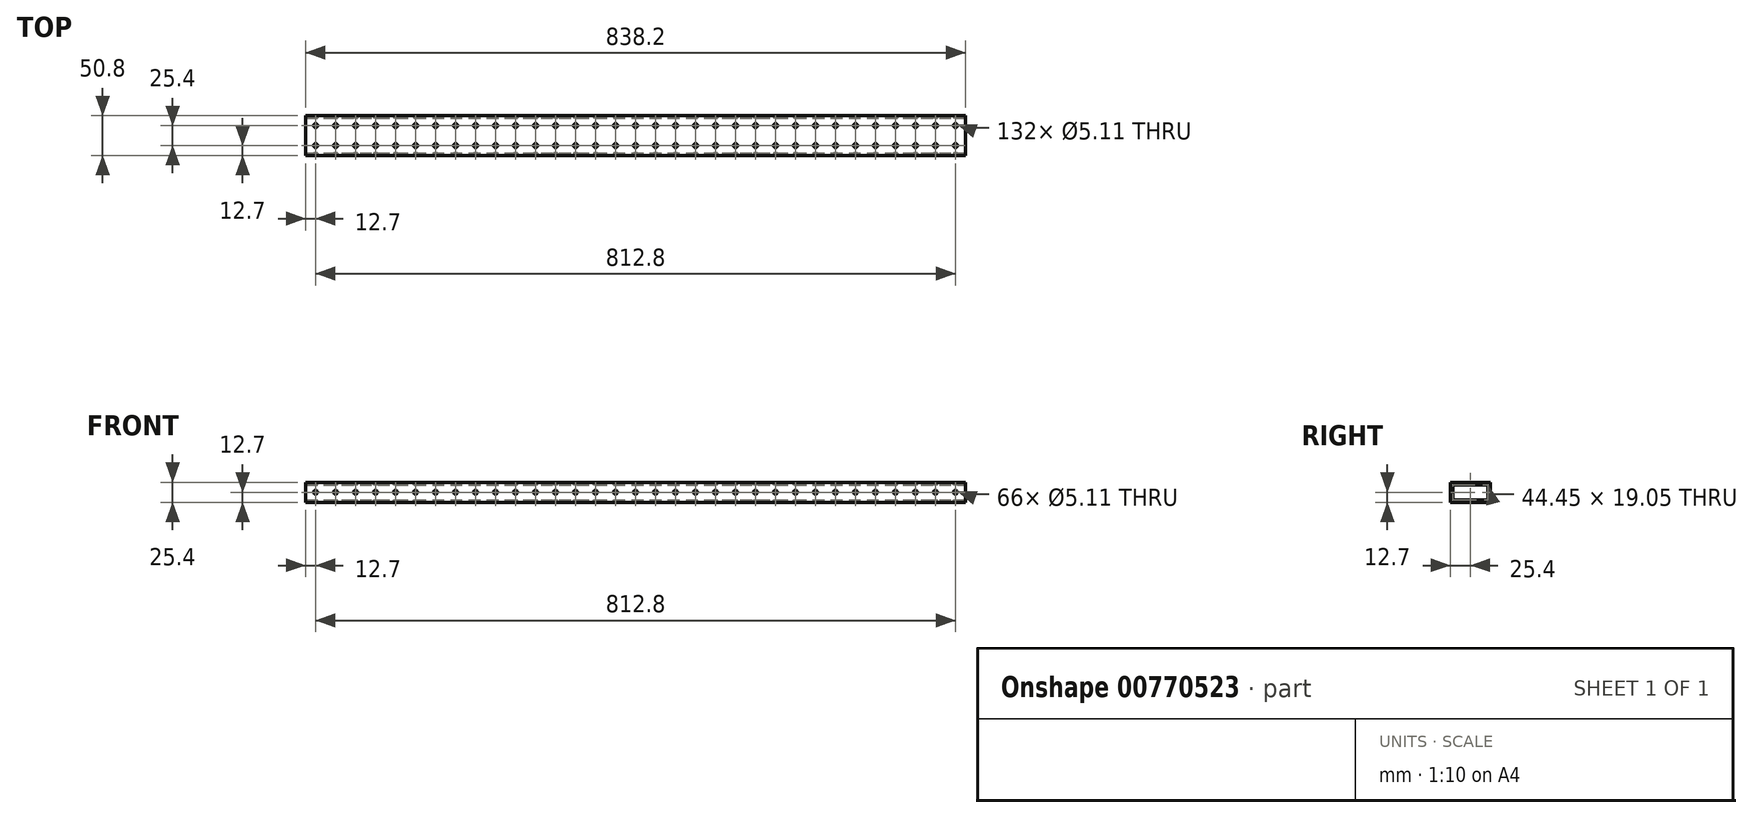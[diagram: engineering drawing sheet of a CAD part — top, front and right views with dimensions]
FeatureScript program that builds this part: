
annotation { "Feature Type Name" : "Feature", "Feature Type Description" : "" }
export const myFeature = defineFeature(function(context is Context, id is Id, definition is map)
    precondition{}
    {
        {
            var Q0;
            Q0=qCreatedBy(makeId("Top.planeOp"),FACE);
            var sketch = newSketch(context, id + "F0", { "sketchPlane" : qUnion([Q0])});
            skLineSegment(sketch, "E0.bottom", {"start": v(419.1, -25.4) * mm, "end": v(-419.1, -25.4) * mm});
            skLineSegment(sketch, "E0.top", {"start": v(419.1, 25.4) * mm, "end": v(-419.1, 25.4) * mm});
            skLineSegment(sketch, "E0.left", {"start": v(419.1, -25.4) * mm, "end": v(419.1, 25.4) * mm});
            skLineSegment(sketch, "E0.right", {"start": v(-419.1, -25.4) * mm, "end": v(-419.1, 25.4) * mm});
            skPoint(sketch, "E0.middle", {"position": v(0, 0) * mm});
            skSolve(sketch);
        }
        {
            var Q0;
            Q0=makeQuery(id+"F0.imprint","IMPRINT",FACE,{"disambiguationData":[TD([[makeQuery(id+"F0.imprint","IMPRINT",EDGE,{"derivedFrom":sQuery(id+"F0.wireOp",EDGE,"E0.bottom")}),-1.0]])]});
            extrude(context, id + "F1", {"entities" : qUnion([Q0]), "depth" : 25.4 * mm, "offsetDistance" : 25.4 * mm});
        }
        {
            var Q0;
            Q0=makeQuery(id+"F1.opExtrude","SWEPT_FACE",FACE,{"disambiguationData":[OSD([sQuery(id+"F0.wireOp",EDGE,"E0.left")])]});
            var sketch = newSketch(context, id + "F2", { "sketchPlane" : qUnion([Q0])});
            skLineSegment(sketch, "E1.0", {"start": v(-22.22, 3.18) * mm, "end": v(22.23, 3.18) * mm});
            skLineSegment(sketch, "E1.1", {"start": v(-22.22, 22.23) * mm, "end": v(-22.22, 3.18) * mm});
            skLineSegment(sketch, "E1.2", {"start": v(22.23, 22.23) * mm, "end": v(-22.22, 22.23) * mm});
            skLineSegment(sketch, "E1.3", {"start": v(22.23, 3.18) * mm, "end": v(22.23, 22.23) * mm});
            skSolve(sketch);
        }
        {
            var Q0;
            Q0=makeQuery(id+"F2.imprint","IMPRINT",FACE,{"disambiguationData":[TD([[makeQuery(id+"F2.imprint","IMPRINT",EDGE,{"derivedFrom":sQuery(id+"F2.wireOp",EDGE,"E1.0")}),1.0]])]});
            extrude(context, id + "F3", {"entities" : qUnion([Q0]), "operationType" : NewBodyOperationType.REMOVE, "oppositeDirection" : true, "depth" : 838.2 * mm, "offsetDistance" : 25.4 * mm});
        }
        {
            var Q0;
            Q0=makeQuery(id+"F1.opExtrude","CAP_FACE",FACE,{"disambiguationData":[OSD([sQuery(id+"F0.wireOp",EDGE,"E0.bottom"),sQuery(id+"F0.wireOp",EDGE,"E0.top"),sQuery(id+"F0.wireOp",EDGE,"E0.left"),sQuery(id+"F0.wireOp",EDGE,"E0.right")])],"isStart":false});
            var sketch = newSketch(context, id + "F4", { "sketchPlane" : qUnion([Q0])});
            skCircle(sketch, "E2", {"center": v(-406.4, 12.7) * mm, "radius": 2.55 * mm});
            skCircle(sketch, "E3.0.1.0", {"center": v(-406.4, -12.7) * mm, "radius": 2.55 * mm});
            skCircle(sketch, "E3.1.0.0", {"center": v(-381, 12.7) * mm, "radius": 2.55 * mm});
            skCircle(sketch, "E3.1.1.0", {"center": v(-381, -12.7) * mm, "radius": 2.55 * mm});
            skCircle(sketch, "E3.2.0.0", {"center": v(-355.6, 12.7) * mm, "radius": 2.55 * mm});
            skCircle(sketch, "E3.2.1.0", {"center": v(-355.6, -12.7) * mm, "radius": 2.55 * mm});
            skCircle(sketch, "E3.3.0.0", {"center": v(-330.2, 12.7) * mm, "radius": 2.55 * mm});
            skCircle(sketch, "E3.3.1.0", {"center": v(-330.2, -12.7) * mm, "radius": 2.55 * mm});
            skCircle(sketch, "E3.4.0.0", {"center": v(-304.8, 12.7) * mm, "radius": 2.55 * mm});
            skCircle(sketch, "E3.4.1.0", {"center": v(-304.8, -12.7) * mm, "radius": 2.55 * mm});
            skCircle(sketch, "E3.5.0.0", {"center": v(-279.4, 12.7) * mm, "radius": 2.55 * mm});
            skCircle(sketch, "E3.5.1.0", {"center": v(-279.4, -12.7) * mm, "radius": 2.55 * mm});
            skCircle(sketch, "E3.6.0.0", {"center": v(-254, 12.7) * mm, "radius": 2.55 * mm});
            skCircle(sketch, "E3.6.1.0", {"center": v(-254, -12.7) * mm, "radius": 2.55 * mm});
            skCircle(sketch, "E3.7.0.0", {"center": v(-228.6, 12.7) * mm, "radius": 2.55 * mm});
            skCircle(sketch, "E3.7.1.0", {"center": v(-228.6, -12.7) * mm, "radius": 2.55 * mm});
            skCircle(sketch, "E3.8.0.0", {"center": v(-203.2, 12.7) * mm, "radius": 2.55 * mm});
            skCircle(sketch, "E3.8.1.0", {"center": v(-203.2, -12.7) * mm, "radius": 2.55 * mm});
            skCircle(sketch, "E3.9.0.0", {"center": v(-177.8, 12.7) * mm, "radius": 2.55 * mm});
            skCircle(sketch, "E3.9.1.0", {"center": v(-177.8, -12.7) * mm, "radius": 2.55 * mm});
            skCircle(sketch, "E3.10.0.0", {"center": v(-152.4, 12.7) * mm, "radius": 2.55 * mm});
            skCircle(sketch, "E3.10.1.0", {"center": v(-152.4, -12.7) * mm, "radius": 2.55 * mm});
            skCircle(sketch, "E3.11.0.0", {"center": v(-127, 12.7) * mm, "radius": 2.55 * mm});
            skCircle(sketch, "E3.11.1.0", {"center": v(-127, -12.7) * mm, "radius": 2.55 * mm});
            skCircle(sketch, "E3.12.0.0", {"center": v(-101.6, 12.7) * mm, "radius": 2.55 * mm});
            skCircle(sketch, "E3.12.1.0", {"center": v(-101.6, -12.7) * mm, "radius": 2.55 * mm});
            skCircle(sketch, "E3.13.0.0", {"center": v(-76.2, 12.7) * mm, "radius": 2.55 * mm});
            skCircle(sketch, "E3.13.1.0", {"center": v(-76.2, -12.7) * mm, "radius": 2.55 * mm});
            skCircle(sketch, "E3.14.0.0", {"center": v(-50.8, 12.7) * mm, "radius": 2.55 * mm});
            skCircle(sketch, "E3.14.1.0", {"center": v(-50.8, -12.7) * mm, "radius": 2.55 * mm});
            skCircle(sketch, "E3.15.0.0", {"center": v(-25.4, 12.7) * mm, "radius": 2.55 * mm});
            skCircle(sketch, "E3.15.1.0", {"center": v(-25.4, -12.7) * mm, "radius": 2.55 * mm});
            skCircle(sketch, "E3.16.0.0", {"center": v(0, 12.7) * mm, "radius": 2.55 * mm});
            skCircle(sketch, "E3.16.1.0", {"center": v(0, -12.7) * mm, "radius": 2.55 * mm});
            skCircle(sketch, "E3.17.0.0", {"center": v(25.4, 12.7) * mm, "radius": 2.55 * mm});
            skCircle(sketch, "E3.17.1.0", {"center": v(25.4, -12.7) * mm, "radius": 2.55 * mm});
            skCircle(sketch, "E3.18.0.0", {"center": v(50.8, 12.7) * mm, "radius": 2.55 * mm});
            skCircle(sketch, "E3.18.1.0", {"center": v(50.8, -12.7) * mm, "radius": 2.55 * mm});
            skCircle(sketch, "E3.19.0.0", {"center": v(76.2, 12.7) * mm, "radius": 2.55 * mm});
            skCircle(sketch, "E3.19.1.0", {"center": v(76.2, -12.7) * mm, "radius": 2.55 * mm});
            skCircle(sketch, "E3.20.0.0", {"center": v(101.6, 12.7) * mm, "radius": 2.55 * mm});
            skCircle(sketch, "E3.20.1.0", {"center": v(101.6, -12.7) * mm, "radius": 2.55 * mm});
            skCircle(sketch, "E3.21.0.0", {"center": v(127, 12.7) * mm, "radius": 2.55 * mm});
            skCircle(sketch, "E3.21.1.0", {"center": v(127, -12.7) * mm, "radius": 2.55 * mm});
            skCircle(sketch, "E3.22.0.0", {"center": v(152.4, 12.7) * mm, "radius": 2.55 * mm});
            skCircle(sketch, "E3.22.1.0", {"center": v(152.4, -12.7) * mm, "radius": 2.55 * mm});
            skCircle(sketch, "E3.23.0.0", {"center": v(177.8, 12.7) * mm, "radius": 2.55 * mm});
            skCircle(sketch, "E3.23.1.0", {"center": v(177.8, -12.7) * mm, "radius": 2.55 * mm});
            skCircle(sketch, "E3.24.0.0", {"center": v(203.2, 12.7) * mm, "radius": 2.55 * mm});
            skCircle(sketch, "E3.24.1.0", {"center": v(203.2, -12.7) * mm, "radius": 2.55 * mm});
            skCircle(sketch, "E3.25.0.0", {"center": v(228.6, 12.7) * mm, "radius": 2.55 * mm});
            skCircle(sketch, "E3.25.1.0", {"center": v(228.6, -12.7) * mm, "radius": 2.55 * mm});
            skCircle(sketch, "E3.26.0.0", {"center": v(254, 12.7) * mm, "radius": 2.55 * mm});
            skCircle(sketch, "E3.26.1.0", {"center": v(254, -12.7) * mm, "radius": 2.55 * mm});
            skCircle(sketch, "E3.27.0.0", {"center": v(279.4, 12.7) * mm, "radius": 2.55 * mm});
            skCircle(sketch, "E3.27.1.0", {"center": v(279.4, -12.7) * mm, "radius": 2.55 * mm});
            skCircle(sketch, "E3.28.0.0", {"center": v(304.8, 12.7) * mm, "radius": 2.55 * mm});
            skCircle(sketch, "E3.28.1.0", {"center": v(304.8, -12.7) * mm, "radius": 2.55 * mm});
            skCircle(sketch, "E3.29.0.0", {"center": v(330.2, 12.7) * mm, "radius": 2.55 * mm});
            skCircle(sketch, "E3.29.1.0", {"center": v(330.2, -12.7) * mm, "radius": 2.55 * mm});
            skCircle(sketch, "E3.30.0.0", {"center": v(355.6, 12.7) * mm, "radius": 2.55 * mm});
            skCircle(sketch, "E3.30.1.0", {"center": v(355.6, -12.7) * mm, "radius": 2.55 * mm});
            skCircle(sketch, "E3.31.0.0", {"center": v(381, 12.7) * mm, "radius": 2.55 * mm});
            skCircle(sketch, "E3.31.1.0", {"center": v(381, -12.7) * mm, "radius": 2.55 * mm});
            skCircle(sketch, "E3.32.0.0", {"center": v(406.4, 12.7) * mm, "radius": 2.55 * mm});
            skCircle(sketch, "E3.32.1.0", {"center": v(406.4, -12.7) * mm, "radius": 2.55 * mm});
            skLineSegment(sketch, "E3.direction1", {"start": v(-406.4, 12.7) * mm, "end": v(-381, 12.7) * mm, "construction": true});
            skLineSegment(sketch, "E3.direction2", {"start": v(-406.4, 12.7) * mm, "end": v(-406.4, -12.7) * mm, "construction": true});
            skSolve(sketch);
        }
        {
            var Q0;
            Q0=sQuery(id+"F4.wireOp",VERTEX,"E3.29.1.0.center");
            var Q1;
            Q1=sQuery(id+"F4.wireOp",VERTEX,"E3.21.1.0.center");
            var Q2;
            Q2=sQuery(id+"F4.wireOp",VERTEX,"E3.13.1.0.center");
            var Q3;
            Q3=sQuery(id+"F4.wireOp",VERTEX,"E3.12.0.0.center");
            var Q4;
            Q4=sQuery(id+"F4.wireOp",VERTEX,"E3.20.0.0.center");
            var Q5;
            Q5=sQuery(id+"F4.wireOp",VERTEX,"E3.28.0.0.center");
            var Q6;
            Q6=sQuery(id+"F4.wireOp",VERTEX,"E3.4.0.0.center");
            var Q7;
            Q7=sQuery(id+"F4.wireOp",VERTEX,"E3.3.1.0.center");
            var Q8;
            Q8=sQuery(id+"F4.wireOp",VERTEX,"E3.3.0.0.center");
            var Q9;
            Q9=sQuery(id+"F4.wireOp",VERTEX,"E3.2.1.0.center");
            var Q10;
            Q10=sQuery(id+"F4.wireOp",VERTEX,"E3.2.0.0.center");
            var Q11;
            Q11=sQuery(id+"F4.wireOp",VERTEX,"E3.1.1.0.center");
            var Q12;
            Q12=sQuery(id+"F4.wireOp",VERTEX,"E3.1.0.0.center");
            var Q13;
            Q13=sQuery(id+"F4.wireOp",VERTEX,"E3.0.1.0.center");
            var Q14;
            Q14=sQuery(id+"F4.wireOp",VERTEX,"E2.center");
            var Q15;
            Q15=sQuery(id+"F4.wireOp",VERTEX,"E3.5.1.0.center");
            var Q16;
            Q16=sQuery(id+"F4.wireOp",VERTEX,"E3.13.0.0.center");
            var Q17;
            Q17=sQuery(id+"F4.wireOp",VERTEX,"E3.21.0.0.center");
            var Q18;
            Q18=sQuery(id+"F4.wireOp",VERTEX,"E3.29.0.0.center");
            var Q19;
            Q19=sQuery(id+"F4.wireOp",VERTEX,"E3.5.0.0.center");
            var Q20;
            Q20=sQuery(id+"F4.wireOp",VERTEX,"E3.4.1.0.center");
            var Q21;
            Q21=sQuery(id+"F4.wireOp",VERTEX,"E3.11.1.0.center");
            var Q22;
            Q22=sQuery(id+"F4.wireOp",VERTEX,"E3.19.1.0.center");
            var Q23;
            Q23=sQuery(id+"F4.wireOp",VERTEX,"E3.27.1.0.center");
            var Q24;
            Q24=sQuery(id+"F4.wireOp",VERTEX,"E3.12.1.0.center");
            var Q25;
            Q25=sQuery(id+"F4.wireOp",VERTEX,"E3.20.1.0.center");
            var Q26;
            Q26=sQuery(id+"F4.wireOp",VERTEX,"E3.28.1.0.center");
            var Q27;
            Q27=sQuery(id+"F4.wireOp",VERTEX,"E3.11.0.0.center");
            var Q28;
            Q28=sQuery(id+"F4.wireOp",VERTEX,"E3.19.0.0.center");
            var Q29;
            Q29=sQuery(id+"F4.wireOp",VERTEX,"E3.27.0.0.center");
            var Q30;
            Q30=sQuery(id+"F4.wireOp",VERTEX,"E3.10.1.0.center");
            var Q31;
            Q31=sQuery(id+"F4.wireOp",VERTEX,"E3.18.1.0.center");
            var Q32;
            Q32=sQuery(id+"F4.wireOp",VERTEX,"E3.26.1.0.center");
            var Q33;
            Q33=sQuery(id+"F4.wireOp",VERTEX,"E3.10.0.0.center");
            var Q34;
            Q34=sQuery(id+"F4.wireOp",VERTEX,"E3.18.0.0.center");
            var Q35;
            Q35=sQuery(id+"F4.wireOp",VERTEX,"E3.26.0.0.center");
            var Q36;
            Q36=sQuery(id+"F4.wireOp",VERTEX,"E3.9.1.0.center");
            var Q37;
            Q37=sQuery(id+"F4.wireOp",VERTEX,"E3.17.1.0.center");
            var Q38;
            Q38=sQuery(id+"F4.wireOp",VERTEX,"E3.25.1.0.center");
            var Q39;
            Q39=sQuery(id+"F4.wireOp",VERTEX,"E3.17.0.0.center");
            var Q40;
            Q40=sQuery(id+"F4.wireOp",VERTEX,"E3.25.0.0.center");
            var Q41;
            Q41=sQuery(id+"F4.wireOp",VERTEX,"E3.9.0.0.center");
            var Q42;
            Q42=sQuery(id+"F4.wireOp",VERTEX,"E3.16.1.0.center");
            var Q43;
            Q43=sQuery(id+"F4.wireOp",VERTEX,"E3.24.1.0.center");
            var Q44;
            Q44=sQuery(id+"F4.wireOp",VERTEX,"E3.32.1.0.center");
            var Q45;
            Q45=sQuery(id+"F4.wireOp",VERTEX,"E3.8.1.0.center");
            var Q46;
            Q46=sQuery(id+"F4.wireOp",VERTEX,"E3.16.0.0.center");
            var Q47;
            Q47=sQuery(id+"F4.wireOp",VERTEX,"E3.24.0.0.center");
            var Q48;
            Q48=sQuery(id+"F4.wireOp",VERTEX,"E3.32.0.0.center");
            var Q49;
            Q49=sQuery(id+"F4.wireOp",VERTEX,"E3.8.0.0.center");
            var Q50;
            Q50=sQuery(id+"F4.wireOp",VERTEX,"E3.15.1.0.center");
            var Q51;
            Q51=sQuery(id+"F4.wireOp",VERTEX,"E3.23.1.0.center");
            var Q52;
            Q52=sQuery(id+"F4.wireOp",VERTEX,"E3.31.1.0.center");
            var Q53;
            Q53=sQuery(id+"F4.wireOp",VERTEX,"E3.7.1.0.center");
            var Q54;
            Q54=sQuery(id+"F4.wireOp",VERTEX,"E3.15.0.0.center");
            var Q55;
            Q55=sQuery(id+"F4.wireOp",VERTEX,"E3.23.0.0.center");
            var Q56;
            Q56=sQuery(id+"F4.wireOp",VERTEX,"E3.31.0.0.center");
            var Q57;
            Q57=sQuery(id+"F4.wireOp",VERTEX,"E3.7.0.0.center");
            var Q58;
            Q58=sQuery(id+"F4.wireOp",VERTEX,"E3.14.1.0.center");
            var Q59;
            Q59=sQuery(id+"F4.wireOp",VERTEX,"E3.22.1.0.center");
            var Q60;
            Q60=sQuery(id+"F4.wireOp",VERTEX,"E3.30.1.0.center");
            var Q61;
            Q61=sQuery(id+"F4.wireOp",VERTEX,"E3.6.1.0.center");
            var Q62;
            Q62=sQuery(id+"F4.wireOp",VERTEX,"E3.14.0.0.center");
            var Q63;
            Q63=sQuery(id+"F4.wireOp",VERTEX,"E3.22.0.0.center");
            var Q64;
            Q64=sQuery(id+"F4.wireOp",VERTEX,"E3.30.0.0.center");
            var Q65;
            Q65=sQuery(id+"F4.wireOp",VERTEX,"E3.6.0.0.center");
            var Q66;
            Q66=makeQuery(id+"F1.opExtrude","SWEPT_BODY",BODY,{"disambiguationData":[OSD([sQuery(id+"F0.wireOp",EDGE,"E0.bottom"),sQuery(id+"F0.wireOp",EDGE,"E0.top"),sQuery(id+"F0.wireOp",EDGE,"E0.left"),sQuery(id+"F0.wireOp",EDGE,"E0.right")])]});
            hole(context, id + "F5", {"style" : HoleStyle.SIMPLE, "endStyle" : HoleEndStyle.BLIND, "holeDiameter" : 5.1 * mm, "majorDiameter" : 6.35 * mm, "holeDepth" : 50.8 * mm, "isTappedThrough" : true, "tappedDepth" : 12.7 * mm, "tapClearance" : 3, "startFromSketch" : true, "locations" : qUnion([Q0, Q1, Q2, Q3, Q4, Q5, Q6, Q7, Q8, Q9, Q10, Q11, Q12, Q13, Q14, Q15, Q16, Q17, Q18, Q19, Q20, Q21, Q22, Q23, Q24, Q25, Q26, Q27, Q28, Q29, Q30, Q31, Q32, Q33, Q34, Q35, Q36, Q37, Q38, Q39, Q40, Q41, Q42, Q43, Q44, Q45, Q46, Q47, Q48, Q49, Q50, Q51, Q52, Q53, Q54, Q55, Q56, Q57, Q58, Q59, Q60, Q61, Q62, Q63, Q64, Q65]), "scope" : qUnion([Q66])});
        }
        {
            var Q0;
            Q0=makeQuery(id+"F1.opExtrude","SWEPT_FACE",FACE,{"disambiguationData":[OSD([sQuery(id+"F0.wireOp",EDGE,"E0.bottom")])]});
            var sketch = newSketch(context, id + "F6", { "sketchPlane" : qUnion([Q0])});
            skCircle(sketch, "E4", {"center": v(-406.4, 12.7) * mm, "radius": 2.55 * mm});
            skCircle(sketch, "E5.1.0.0", {"center": v(-381, 12.7) * mm, "radius": 2.55 * mm});
            skCircle(sketch, "E5.2.0.0", {"center": v(-355.6, 12.7) * mm, "radius": 2.55 * mm});
            skCircle(sketch, "E5.3.0.0", {"center": v(-330.2, 12.7) * mm, "radius": 2.55 * mm});
            skCircle(sketch, "E5.4.0.0", {"center": v(-304.8, 12.7) * mm, "radius": 2.55 * mm});
            skCircle(sketch, "E5.5.0.0", {"center": v(-279.4, 12.7) * mm, "radius": 2.55 * mm});
            skCircle(sketch, "E5.6.0.0", {"center": v(-254, 12.7) * mm, "radius": 2.55 * mm});
            skCircle(sketch, "E5.7.0.0", {"center": v(-228.6, 12.7) * mm, "radius": 2.55 * mm});
            skCircle(sketch, "E5.8.0.0", {"center": v(-203.2, 12.7) * mm, "radius": 2.55 * mm});
            skCircle(sketch, "E5.9.0.0", {"center": v(-177.8, 12.7) * mm, "radius": 2.55 * mm});
            skCircle(sketch, "E5.10.0.0", {"center": v(-152.4, 12.7) * mm, "radius": 2.55 * mm});
            skCircle(sketch, "E5.11.0.0", {"center": v(-127, 12.7) * mm, "radius": 2.55 * mm});
            skCircle(sketch, "E5.12.0.0", {"center": v(-101.6, 12.7) * mm, "radius": 2.55 * mm});
            skCircle(sketch, "E5.13.0.0", {"center": v(-76.2, 12.7) * mm, "radius": 2.55 * mm});
            skCircle(sketch, "E5.14.0.0", {"center": v(-50.8, 12.7) * mm, "radius": 2.55 * mm});
            skCircle(sketch, "E5.15.0.0", {"center": v(-25.4, 12.7) * mm, "radius": 2.55 * mm});
            skCircle(sketch, "E5.16.0.0", {"center": v(0, 12.7) * mm, "radius": 2.55 * mm});
            skCircle(sketch, "E5.17.0.0", {"center": v(25.4, 12.7) * mm, "radius": 2.55 * mm});
            skCircle(sketch, "E5.18.0.0", {"center": v(50.8, 12.7) * mm, "radius": 2.55 * mm});
            skCircle(sketch, "E5.19.0.0", {"center": v(76.2, 12.7) * mm, "radius": 2.55 * mm});
            skCircle(sketch, "E5.20.0.0", {"center": v(101.6, 12.7) * mm, "radius": 2.55 * mm});
            skCircle(sketch, "E5.21.0.0", {"center": v(127, 12.7) * mm, "radius": 2.55 * mm});
            skCircle(sketch, "E5.22.0.0", {"center": v(152.4, 12.7) * mm, "radius": 2.55 * mm});
            skCircle(sketch, "E5.23.0.0", {"center": v(177.8, 12.7) * mm, "radius": 2.55 * mm});
            skCircle(sketch, "E5.24.0.0", {"center": v(203.2, 12.7) * mm, "radius": 2.55 * mm});
            skCircle(sketch, "E5.25.0.0", {"center": v(228.6, 12.7) * mm, "radius": 2.55 * mm});
            skCircle(sketch, "E5.26.0.0", {"center": v(254, 12.7) * mm, "radius": 2.55 * mm});
            skCircle(sketch, "E5.27.0.0", {"center": v(279.4, 12.7) * mm, "radius": 2.55 * mm});
            skCircle(sketch, "E5.28.0.0", {"center": v(304.8, 12.7) * mm, "radius": 2.55 * mm});
            skCircle(sketch, "E5.29.0.0", {"center": v(330.2, 12.7) * mm, "radius": 2.55 * mm});
            skCircle(sketch, "E5.30.0.0", {"center": v(355.6, 12.7) * mm, "radius": 2.55 * mm});
            skCircle(sketch, "E5.31.0.0", {"center": v(381, 12.7) * mm, "radius": 2.55 * mm});
            skCircle(sketch, "E5.32.0.0", {"center": v(406.4, 12.7) * mm, "radius": 2.55 * mm});
            skLineSegment(sketch, "E5.direction1", {"start": v(-406.4, 12.7) * mm, "end": v(-381, 12.7) * mm, "construction": true});
            skSolve(sketch);
        }
        {
            var Q0;
            Q0=sQuery(id+"F6.wireOp",VERTEX,"E5.12.0.0.center");
            var Q1;
            Q1=sQuery(id+"F6.wireOp",VERTEX,"E5.2.0.0.center");
            var Q2;
            Q2=sQuery(id+"F6.wireOp",VERTEX,"E5.26.0.0.center");
            var Q3;
            Q3=sQuery(id+"F6.wireOp",VERTEX,"E5.29.0.0.center");
            var Q4;
            Q4=sQuery(id+"F6.wireOp",VERTEX,"E4.center");
            var Q5;
            Q5=sQuery(id+"F6.wireOp",VERTEX,"E5.11.0.0.center");
            var Q6;
            Q6=sQuery(id+"F6.wireOp",VERTEX,"E5.30.0.0.center");
            var Q7;
            Q7=sQuery(id+"F6.wireOp",VERTEX,"E5.14.0.0.center");
            var Q8;
            Q8=sQuery(id+"F6.wireOp",VERTEX,"E5.1.0.0.center");
            var Q9;
            Q9=sQuery(id+"F6.wireOp",VERTEX,"E5.3.0.0.center");
            var Q10;
            Q10=sQuery(id+"F6.wireOp",VERTEX,"E5.16.0.0.center");
            var Q11;
            Q11=sQuery(id+"F6.wireOp",VERTEX,"E5.32.0.0.center");
            var Q12;
            Q12=sQuery(id+"F6.wireOp",VERTEX,"E5.18.0.0.center");
            var Q13;
            Q13=sQuery(id+"F6.wireOp",VERTEX,"E5.20.0.0.center");
            var Q14;
            Q14=sQuery(id+"F6.wireOp",VERTEX,"E5.25.0.0.center");
            var Q15;
            Q15=sQuery(id+"F6.wireOp",VERTEX,"E5.6.0.0.center");
            var Q16;
            Q16=sQuery(id+"F6.wireOp",VERTEX,"E5.22.0.0.center");
            var Q17;
            Q17=sQuery(id+"F6.wireOp",VERTEX,"E5.8.0.0.center");
            var Q18;
            Q18=sQuery(id+"F6.wireOp",VERTEX,"E5.7.0.0.center");
            var Q19;
            Q19=sQuery(id+"F6.wireOp",VERTEX,"E5.21.0.0.center");
            var Q20;
            Q20=sQuery(id+"F6.wireOp",VERTEX,"E5.28.0.0.center");
            var Q21;
            Q21=sQuery(id+"F6.wireOp",VERTEX,"E5.24.0.0.center");
            var Q22;
            Q22=sQuery(id+"F6.wireOp",VERTEX,"E5.5.0.0.center");
            var Q23;
            Q23=sQuery(id+"F6.wireOp",VERTEX,"E5.27.0.0.center");
            var Q24;
            Q24=sQuery(id+"F6.wireOp",VERTEX,"E5.9.0.0.center");
            var Q25;
            Q25=sQuery(id+"F6.wireOp",VERTEX,"E5.13.0.0.center");
            var Q26;
            Q26=sQuery(id+"F6.wireOp",VERTEX,"E5.23.0.0.center");
            var Q27;
            Q27=sQuery(id+"F6.wireOp",VERTEX,"E5.17.0.0.center");
            var Q28;
            Q28=sQuery(id+"F6.wireOp",VERTEX,"E5.4.0.0.center");
            var Q29;
            Q29=sQuery(id+"F6.wireOp",VERTEX,"E5.19.0.0.center");
            var Q30;
            Q30=sQuery(id+"F6.wireOp",VERTEX,"E5.31.0.0.center");
            var Q31;
            Q31=sQuery(id+"F6.wireOp",VERTEX,"E5.15.0.0.center");
            var Q32;
            Q32=sQuery(id+"F6.wireOp",VERTEX,"E5.10.0.0.center");
            var Q33;
            Q33=makeQuery(id+"F1.opExtrude","SWEPT_BODY",BODY,{"disambiguationData":[OSD([sQuery(id+"F0.wireOp",EDGE,"E0.bottom"),sQuery(id+"F0.wireOp",EDGE,"E0.top"),sQuery(id+"F0.wireOp",EDGE,"E0.left"),sQuery(id+"F0.wireOp",EDGE,"E0.right")])]});
            hole(context, id + "F7", {"style" : HoleStyle.SIMPLE, "endStyle" : HoleEndStyle.BLIND, "holeDiameter" : 5.1 * mm, "majorDiameter" : 6.35 * mm, "holeDepth" : 50.8 * mm, "isTappedThrough" : true, "tappedDepth" : 12.7 * mm, "tapClearance" : 3, "startFromSketch" : true, "locations" : qUnion([Q0, Q1, Q2, Q3, Q4, Q5, Q6, Q7, Q8, Q9, Q10, Q11, Q12, Q13, Q14, Q15, Q16, Q17, Q18, Q19, Q20, Q21, Q22, Q23, Q24, Q25, Q26, Q27, Q28, Q29, Q30, Q31, Q32]), "scope" : qUnion([Q33])});
        }
    });
